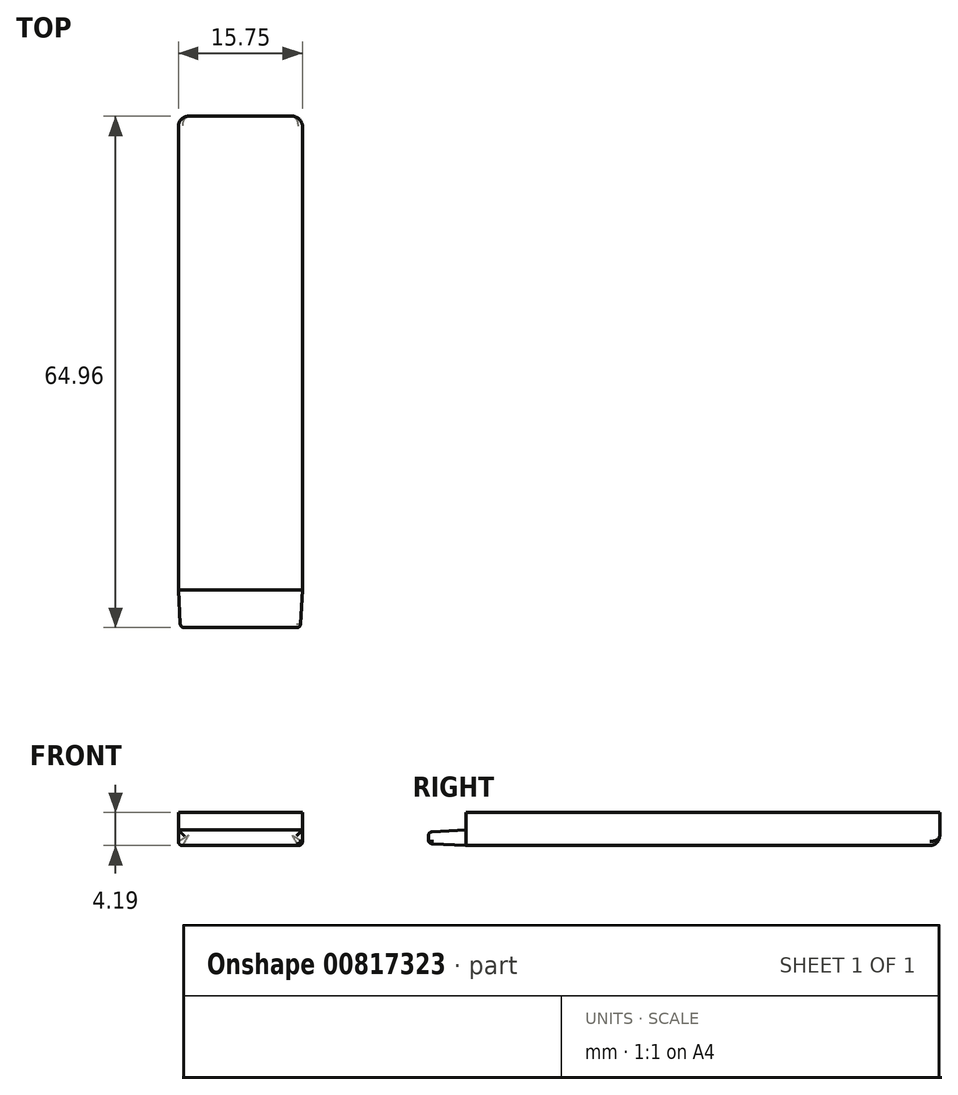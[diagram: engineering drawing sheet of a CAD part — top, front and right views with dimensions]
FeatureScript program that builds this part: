
annotation { "Feature Type Name" : "Feature", "Feature Type Description" : "" }
export const myFeature = defineFeature(function(context is Context, id is Id, definition is map)
    precondition{}
    {
        {
            var Q0;
            Q0=qCreatedBy(makeId("Top.planeOp"),FACE);
            var sketch = newSketch(context, id + "F0", { "sketchPlane" : qUnion([Q0])});
            skLineSegment(sketch, "E0.bottom", {"start": v(-8.44, -19.48) * mm, "end": v(7.3, -19.48) * mm});
            skLineSegment(sketch, "E0.top", {"start": v(-8.44, 40.72) * mm, "end": v(7.3, 40.72) * mm});
            skLineSegment(sketch, "E0.left", {"start": v(-8.44, -19.48) * mm, "end": v(-8.44, 40.72) * mm});
            skLineSegment(sketch, "E0.right", {"start": v(7.3, -19.48) * mm, "end": v(7.3, 40.72) * mm});
            skSolve(sketch);
        }
        {
            var Q0;
            Q0 = qSketchRegion(id + "F0", true);
            extrude(context, id + "F1", {"entities" : qUnion([Q0]), "depth" : 4.2 * mm, "offsetDistance" : 25.4 * mm});
        }
        {
            var Q0;
            Q0=makeQuery(id+"F1.opExtrude","SWEPT_FACE",FACE,{"disambiguationData":[OSD([sQuery(id+"F0.wireOp",EDGE,"E0.bottom")])]});
            var sketch = newSketch(context, id + "F2", { "sketchPlane" : qUnion([Q0])});
            skLineSegment(sketch, "E1.bottom", {"start": v(-8.44, 0) * mm, "end": v(7.3, 0) * mm});
            skLineSegment(sketch, "E1.top", {"start": v(-8.44, 1.98) * mm, "end": v(7.3, 1.98) * mm});
            skLineSegment(sketch, "E1.left", {"start": v(-8.44, 0) * mm, "end": v(-8.44, 1.98) * mm});
            skLineSegment(sketch, "E1.right", {"start": v(7.3, 0) * mm, "end": v(7.3, 1.98) * mm});
            skSolve(sketch);
        }
        {
            var Q0;
            Q0=makeQuery(id+"F2.imprint","IMPRINT",FACE,{"disambiguationData":[TD([[makeQuery(id+"F2.imprint","IMPRINT",EDGE,{"derivedFrom":sQuery(id+"F2.wireOp",EDGE,"E1.bottom")}),1.0]])]});
            extrude(context, id + "F3", {"entities" : qUnion([Q0]), "operationType" : NewBodyOperationType.ADD, "depth" : 4.76 * mm, "offsetDistance" : 25.4 * mm, "hasDraft" : true, "draftAngle" : 3 * degree, "draftPullDirection" : true});
        }
        {
            var Q0;
            Q0=makeQuery(id+"F3.opExtrude","CAP_FACE",FACE,{"disambiguationData":[OSD([sQuery(id+"F2.wireOp",EDGE,"E1.bottom"),sQuery(id+"F2.wireOp",EDGE,"E1.top"),sQuery(id+"F2.wireOp",EDGE,"E1.left"),sQuery(id+"F2.wireOp",EDGE,"E1.right")])],"isStart":false});
            var Q1;
            Q1=makeQuery(id+"F3.opExtrude","SWEPT_EDGE",EDGE,{"disambiguationData":[OSD([sQuery(id+"F2.wireOp",EDGE,"E1.bottom"),sQuery(id+"F2.wireOp",EDGE,"E1.right")])]});
            var Q2;
            Q2=makeQuery(id+"F3.opExtrude","SWEPT_EDGE",EDGE,{"disambiguationData":[OSD([sQuery(id+"F2.wireOp",EDGE,"E1.bottom"),sQuery(id+"F2.wireOp",EDGE,"E1.left")])]});
            var Q3;
            Q3=makeQuery(id+"F3.opExtrude","CAP_EDGE",EDGE,{"disambiguationData":[OSD([sQuery(id+"F2.wireOp",EDGE,"E1.top")])],"isStart":true});
            var Q4;
            Q4=makeQuery(id+"F1.opExtrude","CAP_EDGE",EDGE,{"disambiguationData":[OSD([sQuery(id+"F0.wireOp",EDGE,"E0.right")])],"isStart":true});
            var Q5;
            Q5=makeQuery(id+"F1.opExtrude","CAP_EDGE",EDGE,{"disambiguationData":[OSD([sQuery(id+"F0.wireOp",EDGE,"E0.left")])],"isStart":true});
            fillet(context, id + "F4", {"entities" : qUnion([Q0, Q1, Q2, Q3, Q4, Q5]), "radius" : 0.5 * mm, "allowEdgeOverflow" : false});
        }
        {
            var Q0;
            Q0=makeQuery(id+"F1.opExtrude","CAP_EDGE",EDGE,{"disambiguationData":[OSD([sQuery(id+"F0.wireOp",EDGE,"E0.top")])],"isStart":true});
            fillet(context, id + "F5", {"entities" : qUnion([Q0]), "radius" : 1.27 * mm, "tangentPropagation" : true, "allowEdgeOverflow" : false});
        }
    });
